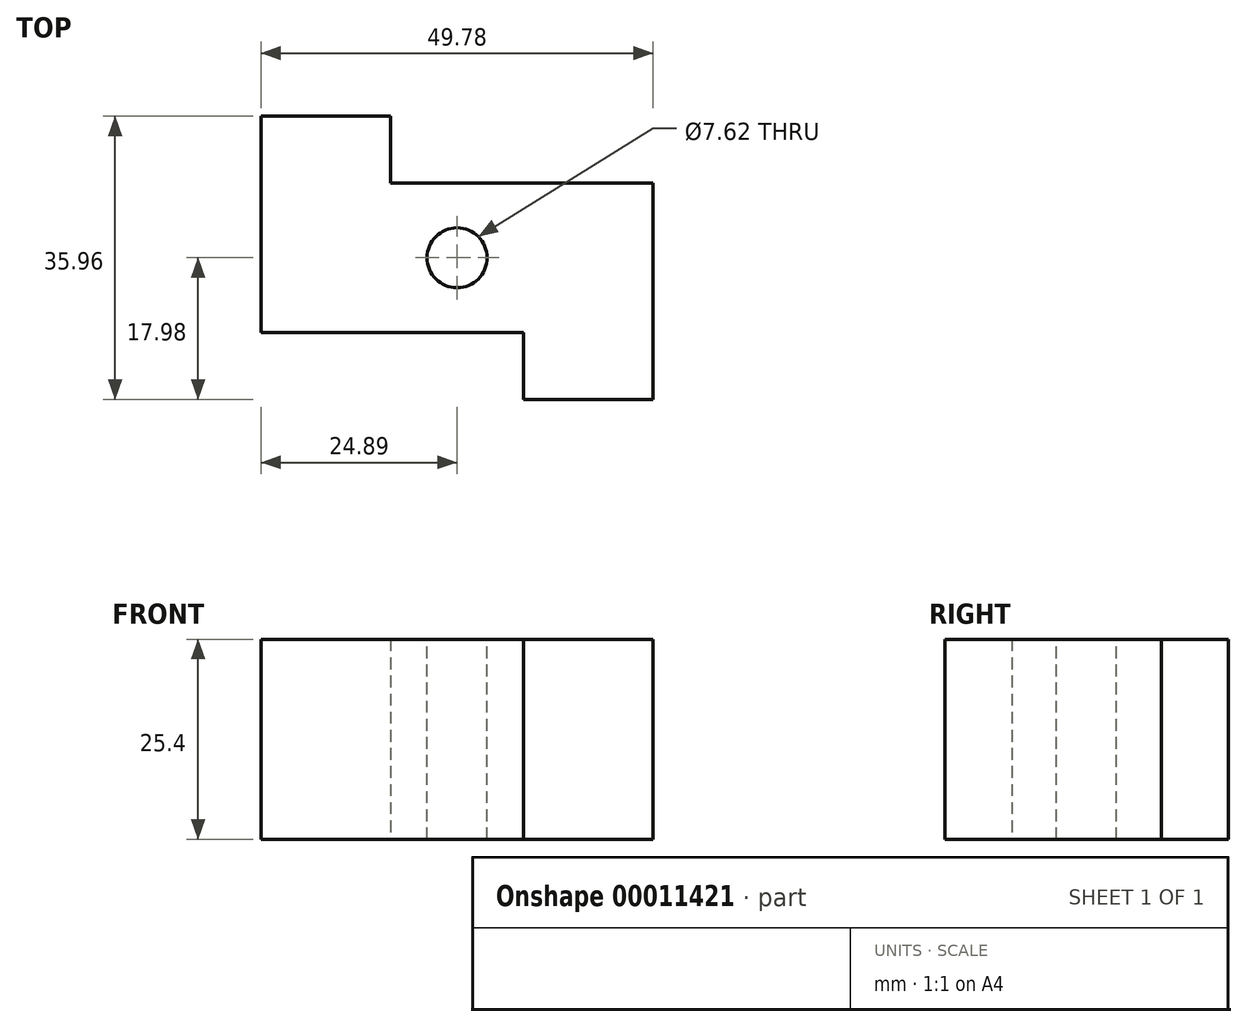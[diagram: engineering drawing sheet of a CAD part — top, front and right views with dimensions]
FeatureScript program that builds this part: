
annotation { "Feature Type Name" : "Feature", "Feature Type Description" : "" }
export const myFeature = defineFeature(function(context is Context, id is Id, definition is map)
    precondition{}
    {
        {
            var Q0;
            Q0=qCreatedBy(makeId("Top.planeOp"),FACE);
            var sketch = newSketch(context, id + "F0", { "sketchPlane" : qUnion([Q0])});
            skLineSegment(sketch, "E0.rect.bottom", {"start": v(-24.9, 17.98) * mm, "end": v(-8.46, 17.98) * mm});
            skLineSegment(sketch, "E0.rect.top", {"start": v(8.46, -17.98) * mm, "end": v(24.9, -17.98) * mm});
            skLineSegment(sketch, "E0.rect.left", {"start": v(-24.9, 17.98) * mm, "end": v(-24.9, -9.47) * mm});
            skLineSegment(sketch, "E0.rect.right", {"start": v(24.9, 9.47) * mm, "end": v(24.9, -17.98) * mm});
            skPoint(sketch, "E0.rect.middle", {"position": v(0, 0) * mm});
            skLineSegment(sketch, "E1", {"start": v(-8.46, 17.98) * mm, "end": v(-8.46, 9.47) * mm});
            skLineSegment(sketch, "E2", {"start": v(-8.46, 9.47) * mm, "end": v(24.9, 9.47) * mm});
            skLineSegment(sketch, "E3", {"start": v(8.46, -17.98) * mm, "end": v(8.46, -9.47) * mm});
            skLineSegment(sketch, "E4", {"start": v(8.46, -9.47) * mm, "end": v(-24.9, -9.47) * mm});
            skPoint(sketch, "E5.orphan", {"position": v(24.9, 17.98) * mm});
            skPoint(sketch, "E6.orphan", {"position": v(-24.9, -17.98) * mm});
            skPoint(sketch, "E7", {"position": v(16.68, -17.98) * mm});
            skSolve(sketch);
        }
        {
            var Q0;
            Q0 = qSketchRegion(id + "F0", true);
            extrude(context, id + "F1", {"entities" : qUnion([Q0]), "depth" : 25.4 * mm});
        }
        {
            var Q0;
            Q0=makeQuery(id+"F1.opExtrude","CAP_FACE",FACE,{"disambiguationData":[OSD([sQuery(id+"F0.wireOp",EDGE,"E0.rect.bottom"),sQuery(id+"F0.wireOp",EDGE,"E0.rect.top"),sQuery(id+"F0.wireOp",EDGE,"E0.rect.left"),sQuery(id+"F0.wireOp",EDGE,"E0.rect.right"),sQuery(id+"F0.wireOp",EDGE,"E1"),sQuery(id+"F0.wireOp",EDGE,"E2"),sQuery(id+"F0.wireOp",EDGE,"E3"),sQuery(id+"F0.wireOp",EDGE,"E4")])],"isStart":false});
            var sketch = newSketch(context, id + "F2", { "sketchPlane" : qUnion([Q0])});
            skCircle(sketch, "E8", {"center": v(0, 0) * mm, "radius": 3.81 * mm});
            skSolve(sketch);
        }
        {
            var Q0;
            Q0 = qSketchRegion(id + "F2", true);
            extrude(context, id + "F3", {"entities" : qUnion([Q0]), "operationType" : NewBodyOperationType.REMOVE, "endBound" : BoundingType.UP_TO_NEXT, "oppositeDirection" : true, "depth" : 25.4 * mm});
        }
    });
